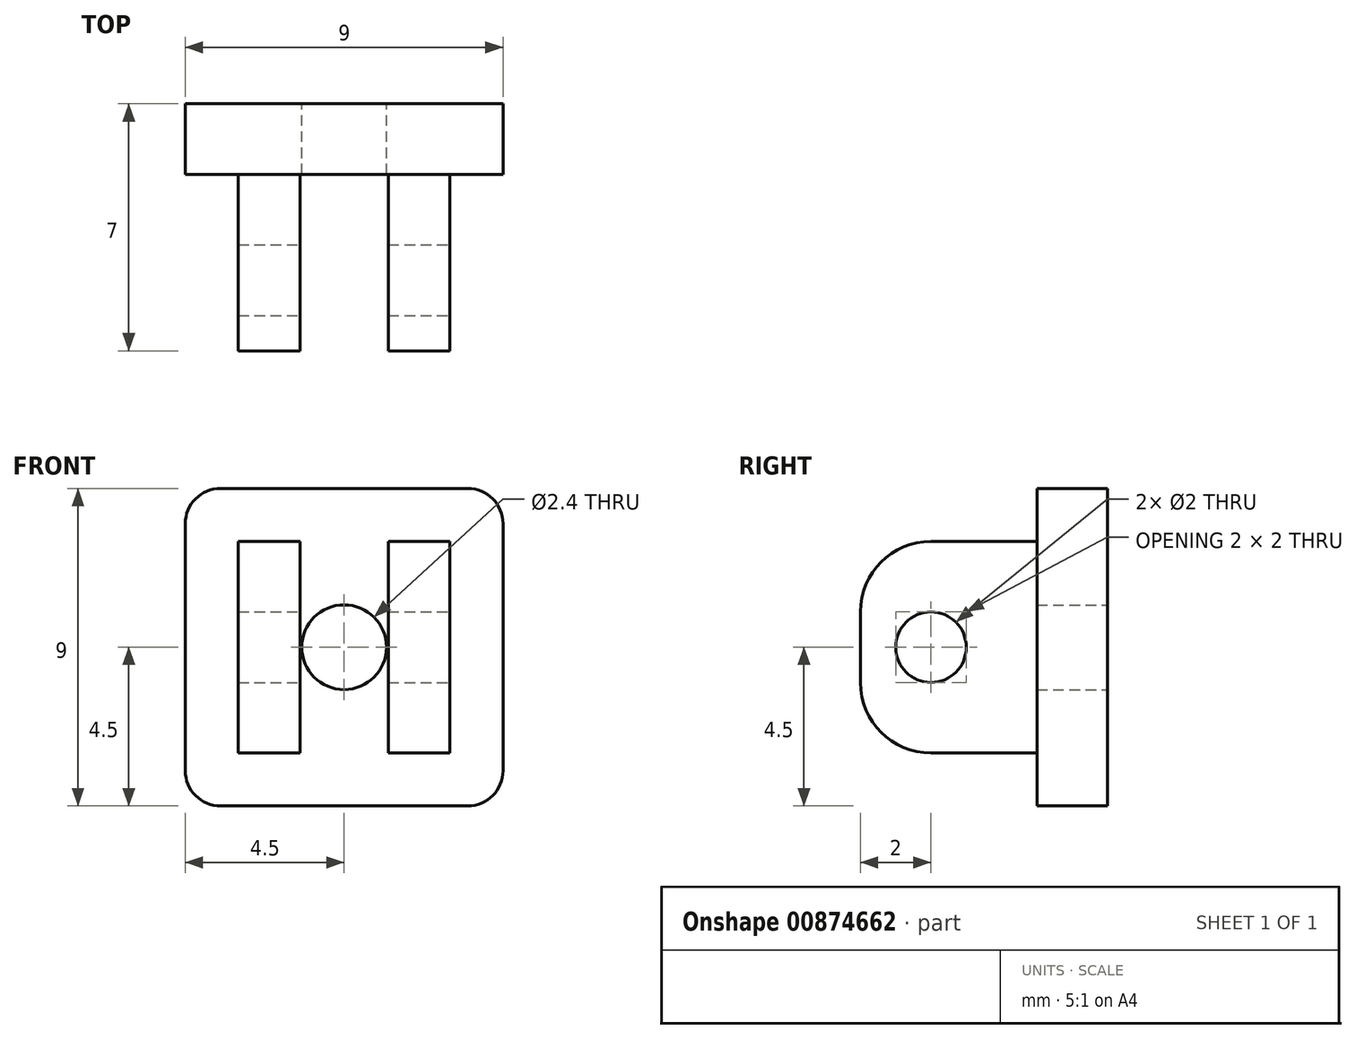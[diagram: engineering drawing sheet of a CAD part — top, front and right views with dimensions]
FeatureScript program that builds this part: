
annotation { "Feature Type Name" : "Feature", "Feature Type Description" : "" }
export const myFeature = defineFeature(function(context is Context, id is Id, definition is map)
    precondition{}
    {
        {
            var Q0;
            Q0=qCreatedBy(makeId("Front.planeOp"),FACE);
            var sketch = newSketch(context, id + "F0", { "sketchPlane" : qUnion([Q0])});
            skLineSegment(sketch, "E0.bottom", {"start": v(3.5, -4.5) * mm, "end": v(-3.5, -4.5) * mm});
            skLineSegment(sketch, "E0.top", {"start": v(3.5, 4.5) * mm, "end": v(-3.5, 4.5) * mm});
            skLineSegment(sketch, "E0.left", {"start": v(4.5, -3.5) * mm, "end": v(4.5, 3.5) * mm});
            skLineSegment(sketch, "E0.right", {"start": v(-4.5, -3.5) * mm, "end": v(-4.5, 3.5) * mm});
            skPoint(sketch, "E0.middle", {"position": v(0, 0) * mm});
            skPoint(sketch, "E1.visualSharp", {"position": v(-4.5, 4.5) * mm});
            skArc(sketch, "E1.filletArc", {"start": v(-3.5, 4.5) * mm, "mid": v(-4.2, 4.2) * mm, "end": v(-4.5, 3.5) * mm});
            skPoint(sketch, "E2.visualSharp", {"position": v(4.5, 4.5) * mm});
            skArc(sketch, "E2.filletArc", {"start": v(4.5, 3.5) * mm, "mid": v(4.2, 4.2) * mm, "end": v(3.5, 4.5) * mm});
            skPoint(sketch, "E3.visualSharp", {"position": v(4.5, -4.5) * mm});
            skArc(sketch, "E3.filletArc", {"start": v(3.5, -4.5) * mm, "mid": v(4.2, -4.2) * mm, "end": v(4.5, -3.5) * mm});
            skPoint(sketch, "E4.visualSharp", {"position": v(-4.5, -4.5) * mm});
            skArc(sketch, "E4.filletArc", {"start": v(-4.5, -3.5) * mm, "mid": v(-4.2, -4.2) * mm, "end": v(-3.5, -4.5) * mm});
            skLineSegment(sketch, "E5.bottom", {"start": v(3, -3) * mm, "end": v(-3, -3) * mm});
            skLineSegment(sketch, "E5.top", {"start": v(3, 3) * mm, "end": v(-3, 3) * mm});
            skLineSegment(sketch, "E5.left", {"start": v(3, -3) * mm, "end": v(3, 3) * mm});
            skLineSegment(sketch, "E5.right", {"start": v(-3, -3) * mm, "end": v(-3, 3) * mm});
            skLineSegment(sketch, "E6.bottom", {"start": v(1.25, -3) * mm, "end": v(-1.25, -3) * mm});
            skLineSegment(sketch, "E6.top", {"start": v(1.25, 3) * mm, "end": v(-1.25, 3) * mm});
            skLineSegment(sketch, "E6.left", {"start": v(1.25, -3) * mm, "end": v(1.25, 3) * mm});
            skLineSegment(sketch, "E6.right", {"start": v(-1.25, -3) * mm, "end": v(-1.25, 3) * mm});
            skCircle(sketch, "E7", {"center": v(0, 0) * mm, "radius": 1.2 * mm});
            skSolve(sketch);
        }
        {
            var Q0;
            Q0=makeQuery(id+"F0.imprint","IMPRINT",FACE,{"disambiguationData":[TD([[makeQuery(id+"F0.imprint","IMPRINT",EDGE,{"derivedFrom":sQuery(id+"F0.wireOp",EDGE,"E0.bottom")}),-1.0]])]});
            var Q1;
            {var subQ1=sQuery(id+"F0.wireOp",EDGE,"E6.left");Q1=makeQuery(id+"F0.imprint","IMPRINT",FACE,{"disambiguationData":[TD([[makeQuery(id+"F0.imprint","IMPRINT",EDGE,{"derivedFrom":subQ1}),1.0]])]});}
            var Q2;
            {var subQ1=sQuery(id+"F0.wireOp",EDGE,"E6.left");Q2=makeQuery(id+"F0.imprint","IMPRINT",FACE,{"disambiguationData":[TD([[makeQuery(id+"F0.imprint","IMPRINT",EDGE,{"derivedFrom":subQ1}),1.0]])]});}
            extrude(context, id + "F1", {"entities" : qUnion([Q0, Q1, Q2]), "depth" : 2 * mm, "offsetDistance" : 25 * mm});
        }
        {
            var Q0;
            {var subQ0=sQuery(id+"F0.wireOp",EDGE,"E5.right");Q0=makeQuery(id+"F0.imprint","IMPRINT",FACE,{"disambiguationData":[TD([[makeQuery(id+"F0.imprint","IMPRINT",EDGE,{"derivedFrom":subQ0}),-1.0]])]});}
            var Q1;
            {var subQ2=sQuery(id+"F0.wireOp",EDGE,"E5.left");Q1=makeQuery(id+"F0.imprint","IMPRINT",FACE,{"disambiguationData":[TD([[makeQuery(id+"F0.imprint","IMPRINT",EDGE,{"derivedFrom":subQ2}),1.0]])]});}
            extrude(context, id + "F2", {"entities" : qUnion([Q0, Q1]), "operationType" : NewBodyOperationType.ADD, "depth" : 7 * mm, "offsetDistance" : 25 * mm});
        }
        {
            var Q0;
            Q0=makeQuery(id+"F2.opExtrude","SWEPT_FACE",FACE,{"disambiguationData":[OSD([sQuery(id+"F0.wireOp",EDGE,"E5.left")])]});
            var sketch = newSketch(context, id + "F3", { "sketchPlane" : qUnion([Q0])});
            skCircle(sketch, "E8", {"center": v(-5, 0) * mm, "radius": 1 * mm});
            skSolve(sketch);
        }
        {
            var Q0;
            Q0 = qSketchRegion(id + "F3", true);
            extrude(context, id + "F4", {"entities" : qUnion([Q0]), "operationType" : NewBodyOperationType.REMOVE, "oppositeDirection" : true, "depth" : 6 * mm, "offsetDistance" : 25 * mm});
        }
        {
            var Q0;
            {var subQ0=sQuery(id+"F0.wireOp",EDGE,"E5.top");Q0=makeQuery(id+"F2.opExtrude","CAP_EDGE",EDGE,{"disambiguationData":[OSD([subQ0]),TDD([makeQuery(id+"F0.imprint","IMPRINT",EDGE,{"disambiguationData":[TD([[makeQuery(id+"F0.imprint","INTERSECT",VERTEX,{"derivedFrom":[subQ0,sQuery(id+"F0.wireOp",EDGE,"E6.left")]}),1.0]])],"derivedFrom":subQ0})])],"isStart":false});}
            fillet(context, id + "F5", {"entities" : qUnion([Q0]), "radius" : 2 * mm, "tangentPropagation" : true, "allowEdgeOverflow" : false});
        }
        {
            var Q0;
            {var subQ0=sQuery(id+"F0.wireOp",EDGE,"E5.top");Q0=makeQuery(id+"F2.opExtrude","CAP_EDGE",EDGE,{"disambiguationData":[OSD([subQ0]),TDD([makeQuery(id+"F0.imprint","IMPRINT",EDGE,{"disambiguationData":[TD([[makeQuery(id+"F0.imprint","INTERSECT",VERTEX,{"derivedFrom":[subQ0,sQuery(id+"F0.wireOp",EDGE,"E5.right")]}),1.0]])],"derivedFrom":subQ0})])],"isStart":false});}
            var Q1;
            {var subQ0=sQuery(id+"F0.wireOp",EDGE,"E5.bottom");Q1=makeQuery(id+"F2.opExtrude","CAP_EDGE",EDGE,{"disambiguationData":[OSD([subQ0]),TDD([makeQuery(id+"F0.imprint","IMPRINT",EDGE,{"disambiguationData":[TD([[makeQuery(id+"F0.imprint","INTERSECT",VERTEX,{"derivedFrom":[subQ0,sQuery(id+"F0.wireOp",EDGE,"E5.right")]}),1.0]])],"derivedFrom":subQ0})])],"isStart":false});}
            var Q2;
            {var subQ0=sQuery(id+"F0.wireOp",EDGE,"E5.bottom");Q2=makeQuery(id+"F2.opExtrude","CAP_EDGE",EDGE,{"disambiguationData":[OSD([subQ0]),TDD([makeQuery(id+"F0.imprint","IMPRINT",EDGE,{"disambiguationData":[TD([[makeQuery(id+"F0.imprint","INTERSECT",VERTEX,{"derivedFrom":[subQ0,sQuery(id+"F0.wireOp",EDGE,"E6.left")]}),1.0]])],"derivedFrom":subQ0})])],"isStart":false});}
            fillet(context, id + "F6", {"entities" : qUnion([Q0, Q1, Q2]), "radius" : 2 * mm, "tangentPropagation" : true, "allowEdgeOverflow" : false});
        }
    });
